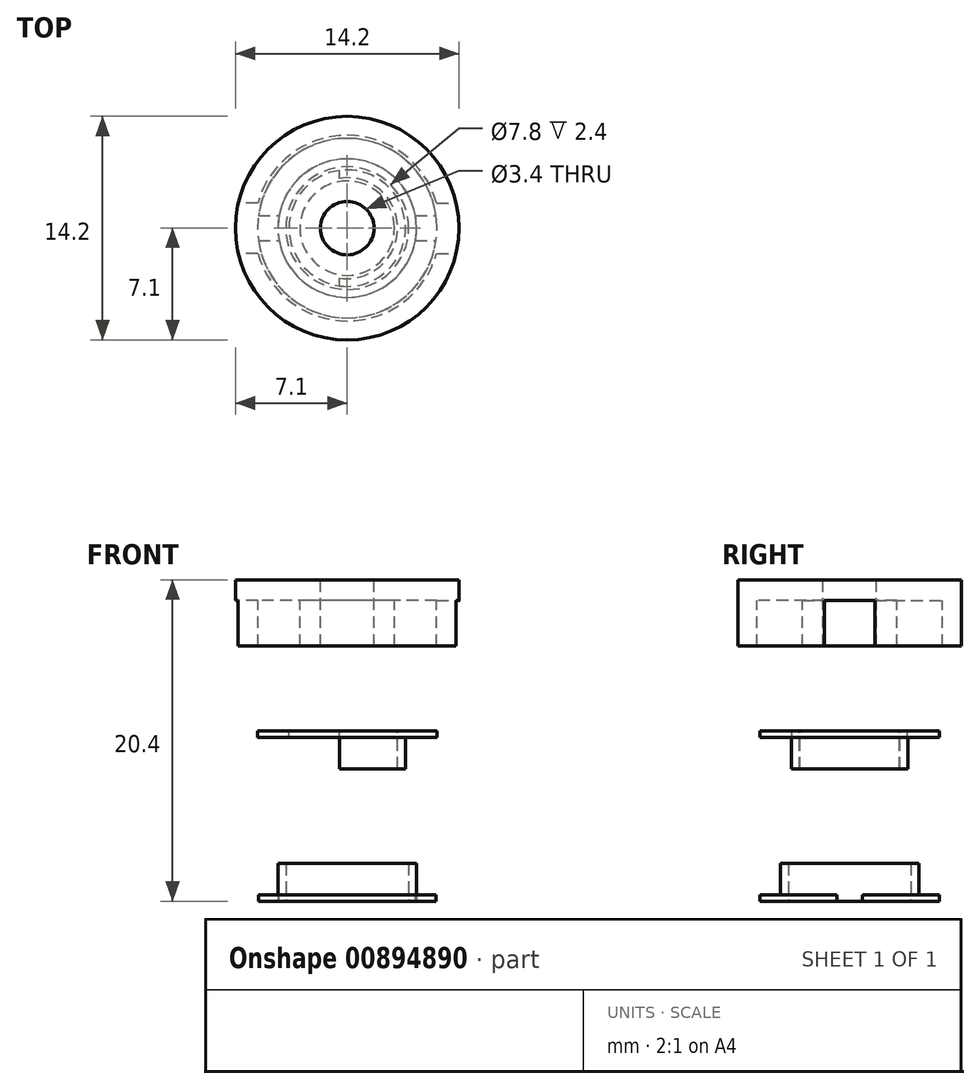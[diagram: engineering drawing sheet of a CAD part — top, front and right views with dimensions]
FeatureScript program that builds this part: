
annotation { "Feature Type Name" : "Feature", "Feature Type Description" : "" }
export const myFeature = defineFeature(function(context is Context, id is Id, definition is map)
    precondition{}
    {
        {
            var Q0;
            Q0=qCreatedBy(makeId("Top.planeOp"),FACE);
            var sketch = newSketch(context, id + "F0", { "sketchPlane" : qUnion([Q0])});
            skCircle(sketch, "E0", {"center": v(0, 0) * mm, "radius": 7.1 * mm});
            skCircle(sketch, "E1", {"center": v(0, 0) * mm, "radius": 5.9 * mm});
            skCircle(sketch, "E2", {"center": v(0, 0) * mm, "radius": 1.7 * mm});
            skCircle(sketch, "E3", {"center": v(0, 0) * mm, "radius": 3 * mm});
            skLineSegment(sketch, "E4.bottom", {"start": v(-7.6, 1.6) * mm, "end": v(7.6, 1.6) * mm, "construction": true});
            skLineSegment(sketch, "E4.top", {"start": v(-7.6, -1.6) * mm, "end": v(7.6, -1.6) * mm, "construction": true});
            skLineSegment(sketch, "E4.left", {"start": v(-7.6, 1.6) * mm, "end": v(-7.6, -1.6) * mm, "construction": true});
            skLineSegment(sketch, "E4.right", {"start": v(7.6, 1.6) * mm, "end": v(7.6, -1.6) * mm, "construction": true});
            skLineSegment(sketch, "E5.bottom", {"start": v(-7.6, 1.6) * mm, "end": v(-5.68, 1.6) * mm});
            skLineSegment(sketch, "E5.top", {"start": v(-7.6, -1.6) * mm, "end": v(-5.68, -1.6) * mm});
            skLineSegment(sketch, "E5.left", {"start": v(-7.6, 1.6) * mm, "end": v(-7.6, -1.6) * mm});
            skLineSegment(sketch, "E5.right", {"start": v(-5.68, 1.6) * mm, "end": v(-5.68, -1.6) * mm});
            skLineSegment(sketch, "E6.bottom", {"start": v(7.6, 1.6) * mm, "end": v(5.68, 1.6) * mm});
            skLineSegment(sketch, "E6.top", {"start": v(7.6, -1.6) * mm, "end": v(5.68, -1.6) * mm});
            skLineSegment(sketch, "E6.left", {"start": v(7.6, 1.6) * mm, "end": v(7.6, -1.6) * mm});
            skLineSegment(sketch, "E6.right", {"start": v(5.68, 1.6) * mm, "end": v(5.68, -1.6) * mm});
            skSolve(sketch);
        }
        {
            var Q0;
            {var subQ0=sQuery(id+"F0.wireOp",EDGE,"E5.bottom");var subQ1=sQuery(id+"F0.wireOp",EDGE,"E0");var subQ2=makeQuery(id+"F0.imprint","INTERSECT",VERTEX,{"derivedFrom":[subQ1,subQ0]});Q0=makeQuery(id+"F0.imprint","IMPRINT",FACE,{"disambiguationData":[TD([[makeQuery(id+"F0.imprint","IMPRINT",EDGE,{"disambiguationData":[TD([[subQ2,1.0]])],"derivedFrom":subQ1}),1.0]])]});}
            var Q1;
            {var subQ0=sQuery(id+"F0.wireOp",EDGE,"E5.top");var subQ1=sQuery(id+"F0.wireOp",EDGE,"E0");var subQ2=makeQuery(id+"F0.imprint","INTERSECT",VERTEX,{"derivedFrom":[subQ1,subQ0]});Q1=makeQuery(id+"F0.imprint","IMPRINT",FACE,{"disambiguationData":[TD([[makeQuery(id+"F0.imprint","IMPRINT",EDGE,{"disambiguationData":[TD([[subQ2,-1.0]])],"derivedFrom":subQ1}),1.0]])]});}
            var Q2;
            Q2=makeQuery(id+"F0.imprint","IMPRINT",FACE,{"disambiguationData":[TD([[makeQuery(id+"F0.imprint","IMPRINT",EDGE,{"derivedFrom":sQuery(id+"F0.wireOp",EDGE,"E2")}),-1.0]])]});
            extrude(context, id + "F1", {"entities" : qUnion([Q0, Q1, Q2]), "oppositeDirection" : true, "depth" : 4.2 * mm, "offsetDistance" : 25 * mm});
        }
        {
            var Q0;
            Q0=makeQuery(id+"F0.imprint","IMPRINT",FACE,{"disambiguationData":[TD([[makeQuery(id+"F0.imprint","IMPRINT",EDGE,{"derivedFrom":sQuery(id+"F0.wireOp",EDGE,"E0")}),1.0]])]});
            var Q1;
            Q1=makeQuery(id+"F0.imprint","IMPRINT",FACE,{"disambiguationData":[TD([[makeQuery(id+"F0.imprint","IMPRINT",EDGE,{"derivedFrom":sQuery(id+"F0.wireOp",EDGE,"E1")}),1.0]])]});
            var Q2;
            {var subQ0=sQuery(id+"F0.wireOp",EDGE,"E5.right");Q2=makeQuery(id+"F0.imprint","IMPRINT",FACE,{"disambiguationData":[TD([[makeQuery(id+"F0.imprint","IMPRINT",EDGE,{"derivedFrom":subQ0}),-1.0]])]});}
            var Q3;
            {var subQ0=sQuery(id+"F0.wireOp",EDGE,"E6.right");Q3=makeQuery(id+"F0.imprint","IMPRINT",FACE,{"disambiguationData":[TD([[makeQuery(id+"F0.imprint","IMPRINT",EDGE,{"derivedFrom":subQ0}),1.0]])]});}
            extrude(context, id + "F2", {"entities" : qUnion([Q0, Q1, Q2, Q3]), "operationType" : NewBodyOperationType.ADD, "oppositeDirection" : true, "depth" : 1.3 * mm, "offsetDistance" : 25 * mm});
        }
        {
            var Q0;
            Q0=qCreatedBy(makeId("Top.planeOp"),FACE);
            cPlane(context, id + "F3", {"entities" : qUnion([Q0]), "cplaneType" : CPlaneType.OFFSET, "offset" : 10 * mm, "oppositeDirection" : true, "width" : 150 * mm, "height" : 150 * mm});
        }
        {
            var Q0;
            Q0=qCreatedBy(id+"F3.planeOp",FACE);
            var sketch = newSketch(context, id + "F4", { "sketchPlane" : qUnion([Q0])});
            skCircle(sketch, "E7", {"center": v(0, 0) * mm, "radius": 3.2 * mm});
            skCircle(sketch, "E8", {"center": v(0, 0) * mm, "radius": 5.7 * mm});
            skCircle(sketch, "E9", {"center": v(0, 0) * mm, "radius": 3.7 * mm});
            skLineSegment(sketch, "E10.bottom", {"start": v(-0.5, -4.33) * mm, "end": v(0.5, -4.33) * mm});
            skLineSegment(sketch, "E10.top", {"start": v(-0.5, 4.33) * mm, "end": v(0.5, 4.33) * mm});
            skLineSegment(sketch, "E10.left", {"start": v(-0.5, -4.33) * mm, "end": v(-0.5, 4.33) * mm});
            skLineSegment(sketch, "E10.right", {"start": v(0.5, -4.33) * mm, "end": v(0.5, 4.33) * mm});
            skSolve(sketch);
        }
        {
            var Q0;
            Q0=makeQuery(id+"F4.imprint","IMPRINT",FACE,{"disambiguationData":[TD([[makeQuery(id+"F4.imprint","IMPRINT",EDGE,{"derivedFrom":sQuery(id+"F4.wireOp",EDGE,"E7")}),-1.0]])]});
            extrude(context, id + "F5", {"entities" : qUnion([Q0]), "oppositeDirection" : true, "depth" : 2 * mm, "offsetDistance" : 25 * mm});
        }
        {
            var Q0;
            Q0=makeQuery(id+"F4.imprint","IMPRINT",FACE,{"disambiguationData":[TD([[makeQuery(id+"F4.imprint","IMPRINT",EDGE,{"derivedFrom":sQuery(id+"F4.wireOp",EDGE,"E7")}),-1.0]])]});
            var Q1;
            Q1=makeQuery(id+"F4.imprint","IMPRINT",FACE,{"disambiguationData":[TD([[makeQuery(id+"F4.imprint","IMPRINT",EDGE,{"derivedFrom":sQuery(id+"F4.wireOp",EDGE,"E8")}),1.0]])]});
            var Q2;
            {var subQ5=sQuery(id+"F4.wireOp",EDGE,"E10.top");Q2=makeQuery(id+"F4.imprint","IMPRINT",FACE,{"disambiguationData":[TD([[makeQuery(id+"F4.imprint","IMPRINT",EDGE,{"derivedFrom":subQ5}),-1.0]])]});}
            var Q3;
            {var subQ5=sQuery(id+"F4.wireOp",EDGE,"E10.bottom");Q3=makeQuery(id+"F4.imprint","IMPRINT",FACE,{"disambiguationData":[TD([[makeQuery(id+"F4.imprint","IMPRINT",EDGE,{"derivedFrom":subQ5}),1.0]])]});}
            extrude(context, id + "F6", {"entities" : qUnion([Q0, Q1, Q2, Q3]), "operationType" : NewBodyOperationType.ADD, "depth" : 0.4 * mm, "offsetDistance" : 25 * mm});
        }
        {
            var Q0;
            {var subQ0=sQuery(id+"F4.wireOp",EDGE,"E10.left");var subQ1=sQuery(id+"F4.wireOp",EDGE,"E7");var subQ2=makeQuery(id+"F4.imprint","INTERSECT",VERTEX,{"disambiguationData":[OD(0.0)],"derivedFrom":[subQ1,subQ0]});Q0=makeQuery(id+"F4.imprint","IMPRINT",FACE,{"disambiguationData":[TD([[makeQuery(id+"F4.imprint","IMPRINT",EDGE,{"disambiguationData":[TD([[subQ2,1.0]])],"derivedFrom":subQ1}),-1.0]])]});}
            var Q1;
            {var subQ0=sQuery(id+"F4.wireOp",EDGE,"E10.left");var subQ1=sQuery(id+"F4.wireOp",EDGE,"E7");var subQ2=makeQuery(id+"F4.imprint","INTERSECT",VERTEX,{"disambiguationData":[OD(1.0)],"derivedFrom":[subQ1,subQ0]});Q1=makeQuery(id+"F4.imprint","IMPRINT",FACE,{"disambiguationData":[TD([[makeQuery(id+"F4.imprint","IMPRINT",EDGE,{"disambiguationData":[TD([[subQ2,-1.0]])],"derivedFrom":subQ1}),-1.0]])]});}
            extrude(context, id + "F7", {"entities" : qUnion([Q0, Q1]), "operationType" : NewBodyOperationType.REMOVE, "endBound" : BoundingType.SYMMETRIC, "oppositeDirection" : true, "depth" : 4 * mm, "offsetDistance" : 25 * mm});
        }
        {
            var Q0;
            Q0=qCreatedBy(makeId("Top.planeOp"),FACE);
            cPlane(context, id + "F8", {"entities" : qUnion([Q0]), "cplaneType" : CPlaneType.OFFSET, "offset" : 20 * mm, "oppositeDirection" : true, "width" : 150 * mm, "height" : 150 * mm});
        }
        {
            var Q0;
            Q0=qCreatedBy(id+"F8.planeOp",FACE);
            var sketch = newSketch(context, id + "F9", { "sketchPlane" : qUnion([Q0])});
            skCircle(sketch, "E11.0", {"center": v(0, 0) * mm, "radius": 5.7 * mm});
            skCircle(sketch, "E12", {"center": v(0, 0) * mm, "radius": 3.9 * mm});
            skCircle(sketch, "E13", {"center": v(0, 0) * mm, "radius": 4.4 * mm});
            skLineSegment(sketch, "E14.bottom", {"start": v(-8.13, -0.8) * mm, "end": v(8.13, -0.8) * mm});
            skLineSegment(sketch, "E14.top", {"start": v(-8.13, 0.8) * mm, "end": v(8.13, 0.8) * mm});
            skLineSegment(sketch, "E14.left", {"start": v(-8.13, -0.8) * mm, "end": v(-8.13, 0.8) * mm});
            skLineSegment(sketch, "E14.right", {"start": v(8.13, -0.8) * mm, "end": v(8.13, 0.8) * mm});
            skSolve(sketch);
        }
        {
            var Q0;
            Q0=makeQuery(id+"F9.imprint","IMPRINT",FACE,{"disambiguationData":[TD([[makeQuery(id+"F9.imprint","IMPRINT",EDGE,{"derivedFrom":sQuery(id+"F9.wireOp",EDGE,"E12")}),-1.0]])]});
            extrude(context, id + "F10", {"entities" : qUnion([Q0]), "depth" : 2 * mm, "offsetDistance" : 25 * mm});
        }
        {
            var Q0;
            {var subQ0=sQuery(id+"F9.wireOp",EDGE,"E14.top");var subQ1=sQuery(id+"F9.wireOp",EDGE,"E11.0");var subQ2=makeQuery(id+"F9.imprint","INTERSECT",VERTEX,{"disambiguationData":[OD(0.0)],"derivedFrom":[subQ1,subQ0]});Q0=makeQuery(id+"F9.imprint","IMPRINT",FACE,{"disambiguationData":[TD([[makeQuery(id+"F9.imprint","IMPRINT",EDGE,{"disambiguationData":[TD([[subQ2,1.0]])],"derivedFrom":subQ1}),1.0]])]});}
            var Q1;
            {var subQ0=sQuery(id+"F9.wireOp",EDGE,"E14.bottom");var subQ1=sQuery(id+"F9.wireOp",EDGE,"E11.0");var subQ2=makeQuery(id+"F9.imprint","INTERSECT",VERTEX,{"disambiguationData":[OD(0.0)],"derivedFrom":[subQ1,subQ0]});Q1=makeQuery(id+"F9.imprint","IMPRINT",FACE,{"disambiguationData":[TD([[makeQuery(id+"F9.imprint","IMPRINT",EDGE,{"disambiguationData":[TD([[subQ2,-1.0]])],"derivedFrom":subQ1}),1.0]])]});}
            var Q2;
            {var subQ0=sQuery(id+"F9.wireOp",EDGE,"E14.top");var subQ1=sQuery(id+"F9.wireOp",EDGE,"E12");var subQ2=makeQuery(id+"F9.imprint","INTERSECT",VERTEX,{"disambiguationData":[OD(0.0)],"derivedFrom":[subQ1,subQ0]});Q2=makeQuery(id+"F9.imprint","IMPRINT",FACE,{"disambiguationData":[TD([[makeQuery(id+"F9.imprint","IMPRINT",EDGE,{"disambiguationData":[TD([[subQ2,1.0]])],"derivedFrom":subQ1}),-1.0]])]});}
            var Q3;
            {var subQ0=sQuery(id+"F9.wireOp",EDGE,"E14.top");var subQ1=sQuery(id+"F9.wireOp",EDGE,"E12");var subQ2=makeQuery(id+"F9.imprint","INTERSECT",VERTEX,{"disambiguationData":[OD(0.0)],"derivedFrom":[subQ1,subQ0]});Q3=makeQuery(id+"F9.imprint","IMPRINT",FACE,{"disambiguationData":[TD([[makeQuery(id+"F9.imprint","IMPRINT",EDGE,{"disambiguationData":[TD([[subQ2,-1.0]])],"derivedFrom":subQ1}),-1.0]])]});}
            var Q4;
            {var subQ0=sQuery(id+"F9.wireOp",EDGE,"E14.top");var subQ1=sQuery(id+"F9.wireOp",EDGE,"E12");var subQ2=makeQuery(id+"F9.imprint","INTERSECT",VERTEX,{"disambiguationData":[OD(1.0)],"derivedFrom":[subQ1,subQ0]});Q4=makeQuery(id+"F9.imprint","IMPRINT",FACE,{"disambiguationData":[TD([[makeQuery(id+"F9.imprint","IMPRINT",EDGE,{"disambiguationData":[TD([[subQ2,1.0]])],"derivedFrom":subQ1}),-1.0]])]});}
            var Q5;
            {var subQ0=sQuery(id+"F9.wireOp",EDGE,"E14.bottom");var subQ1=sQuery(id+"F9.wireOp",EDGE,"E12");var subQ2=makeQuery(id+"F9.imprint","INTERSECT",VERTEX,{"disambiguationData":[OD(0.0)],"derivedFrom":[subQ1,subQ0]});Q5=makeQuery(id+"F9.imprint","IMPRINT",FACE,{"disambiguationData":[TD([[makeQuery(id+"F9.imprint","IMPRINT",EDGE,{"disambiguationData":[TD([[subQ2,-1.0]])],"derivedFrom":subQ1}),-1.0]])]});}
            extrude(context, id + "F11", {"entities" : qUnion([Q0, Q1, Q2, Q3, Q4, Q5]), "operationType" : NewBodyOperationType.ADD, "oppositeDirection" : true, "depth" : 0.4 * mm, "offsetDistance" : 25 * mm});
        }
    });
